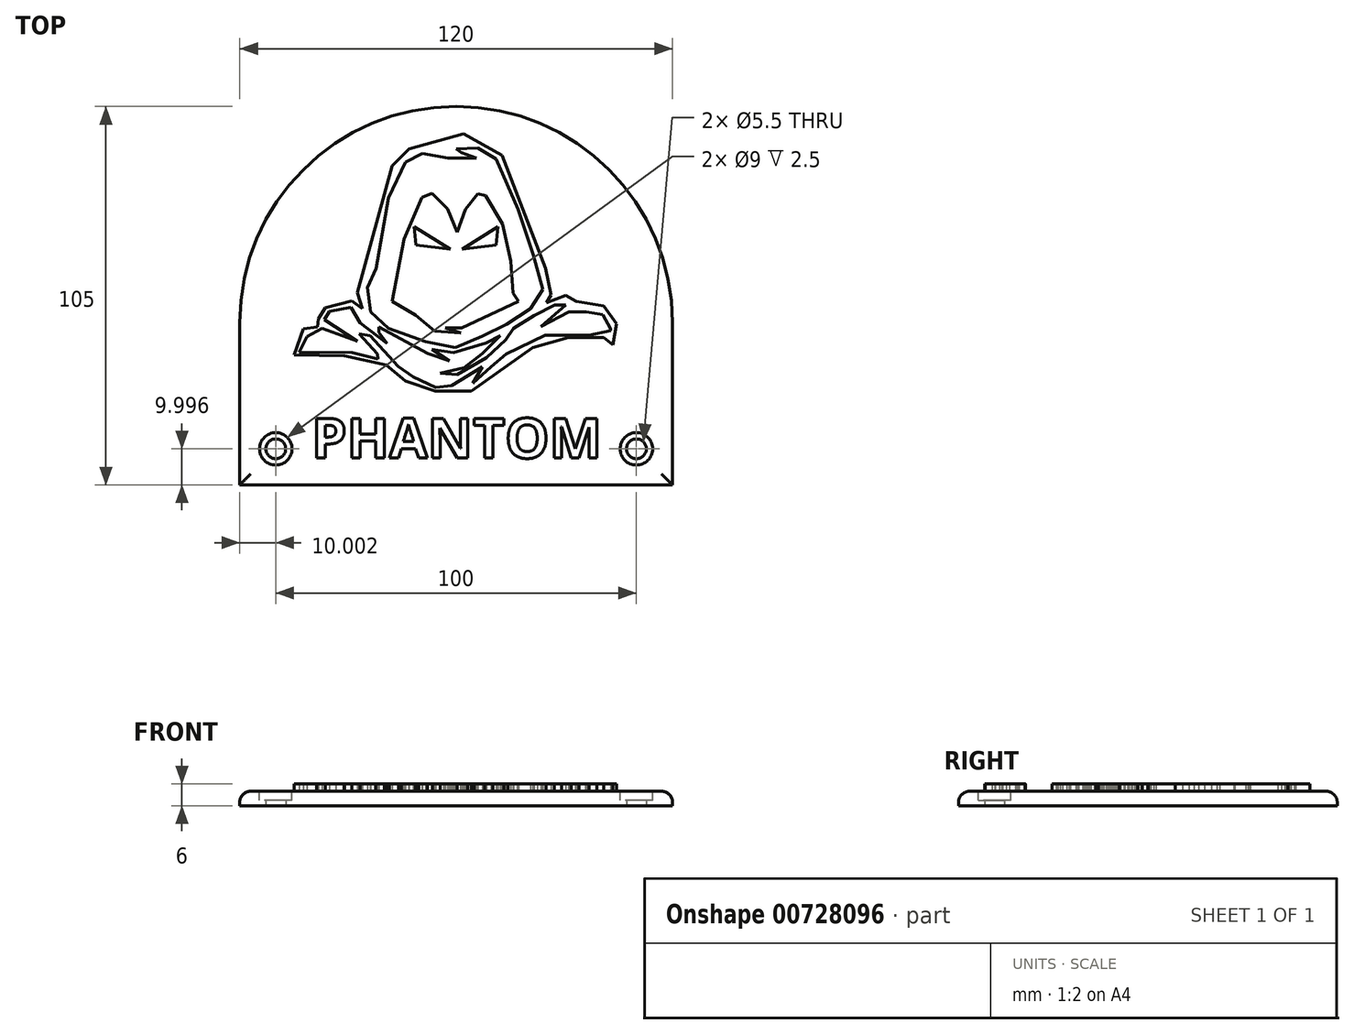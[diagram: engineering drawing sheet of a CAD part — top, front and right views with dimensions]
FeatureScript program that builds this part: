
annotation { "Feature Type Name" : "Feature", "Feature Type Description" : "" }
export const myFeature = defineFeature(function(context is Context, id is Id, definition is map)
    precondition{}
    {
        {
            var Q0;
            Q0=qCreatedBy(makeId("Top.planeOp"),FACE);
            var sketch = newSketch(context, id + "F0", { "sketchPlane" : qUnion([Q0])});
            skLineSegment(sketch, "E0", {"start": v(0.61, 84.34) * mm, "end": v(0.61, -59.17) * mm, "construction": true});
            skLineSegment(sketch, "E1", {"start": v(-44.33, 15.39) * mm, "end": v(-41.76, 22.7) * mm});
            skLineSegment(sketch, "E2", {"start": v(-41.76, 22.7) * mm, "end": v(-37.82, 23.18) * mm});
            skLineSegment(sketch, "E3", {"start": v(-37.82, 23.18) * mm, "end": v(-37.51, 25.44) * mm});
            skLineSegment(sketch, "E4", {"start": v(-37.51, 25.44) * mm, "end": v(-35.7, 28.5) * mm});
            skLineSegment(sketch, "E5", {"start": v(-26.83, 32.69) * mm, "end": v(-17.13, 67.8) * mm});
            skLineSegment(sketch, "E6", {"start": v(-17.13, 67.8) * mm, "end": v(-12.44, 72.5) * mm});
            skLineSegment(sketch, "E7", {"start": v(-12.44, 72.5) * mm, "end": v(2.64, 76.76) * mm});
            skLineSegment(sketch, "E8", {"start": v(2.64, 76.76) * mm, "end": v(13.31, 70.7) * mm});
            skLineSegment(sketch, "E9", {"start": v(13.31, 70.7) * mm, "end": v(25.4, 39.43) * mm});
            skLineSegment(sketch, "E10", {"start": v(25.4, 39.43) * mm, "end": v(26.91, 32) * mm});
            skLineSegment(sketch, "E11", {"start": v(31, 31.86) * mm, "end": v(33.88, 30.23) * mm});
            skLineSegment(sketch, "E12", {"start": v(33.88, 30.23) * mm, "end": v(41.55, 29.03) * mm});
            skLineSegment(sketch, "E13", {"start": v(41.55, 29.03) * mm, "end": v(45.06, 23.98) * mm});
            skLineSegment(sketch, "E14", {"start": v(45.06, 23.98) * mm, "end": v(44.14, 18.15) * mm});
            skLineSegment(sketch, "E15", {"start": v(44.14, 18.15) * mm, "end": v(41.5, 20.21) * mm});
            skLineSegment(sketch, "E16", {"start": v(41.5, 20.21) * mm, "end": v(31.77, 20.21) * mm});
            skLineSegment(sketch, "E17", {"start": v(31.77, 20.21) * mm, "end": v(21.89, 17.46) * mm});
            skLineSegment(sketch, "E18", {"start": v(21.89, 17.46) * mm, "end": v(4.8, 5.31) * mm});
            skLineSegment(sketch, "E19", {"start": v(4.8, 5.31) * mm, "end": v(-5.19, 5.31) * mm});
            skLineSegment(sketch, "E20", {"start": v(-5.19, 5.31) * mm, "end": v(-13.4, 8.22) * mm});
            skLineSegment(sketch, "E21", {"start": v(-13.4, 8.22) * mm, "end": v(-18.73, 12.62) * mm});
            skLineSegment(sketch, "E22", {"start": v(-18.73, 12.62) * mm, "end": v(-30.3, 15.17) * mm});
            skLineSegment(sketch, "E23", {"start": v(-30.3, 15.17) * mm, "end": v(-44.33, 15.39) * mm});
            skLineSegment(sketch, "E24", {"start": v(0.61, 72.55) * mm, "end": v(6.59, 72.8) * mm});
            skLineSegment(sketch, "E25", {"start": v(6.59, 72.8) * mm, "end": v(11.77, 69.75) * mm});
            skLineSegment(sketch, "E26", {"start": v(11.77, 69.75) * mm, "end": v(17.81, 55.78) * mm});
            skLineSegment(sketch, "E27", {"start": v(17.81, 55.78) * mm, "end": v(21.98, 43.27) * mm});
            skLineSegment(sketch, "E28", {"start": v(21.98, 43.27) * mm, "end": v(24.67, 33.51) * mm});
            skLineSegment(sketch, "E29", {"start": v(24.67, 33.51) * mm, "end": v(21.25, 28.17) * mm});
            skLineSegment(sketch, "E30", {"start": v(21.25, 28.17) * mm, "end": v(14.66, 23.95) * mm});
            skLineSegment(sketch, "E31", {"start": v(14.66, 23.95) * mm, "end": v(7.96, 20.56) * mm});
            skLineSegment(sketch, "E32", {"start": v(7.96, 20.56) * mm, "end": v(0.4, 17.4) * mm});
            skLineSegment(sketch, "E33", {"start": v(0.4, 17.4) * mm, "end": v(-7.82, 19.08) * mm});
            skLineSegment(sketch, "E34", {"start": v(-7.82, 19.08) * mm, "end": v(-18.1, 22.8) * mm});
            skLineSegment(sketch, "E35", {"start": v(-18.1, 22.8) * mm, "end": v(-23.1, 27.36) * mm});
            skLineSegment(sketch, "E36", {"start": v(-23.1, 27.36) * mm, "end": v(-23.94, 34.05) * mm});
            skLineSegment(sketch, "E37", {"start": v(-23.94, 34.05) * mm, "end": v(-21.53, 39.35) * mm});
            skLineSegment(sketch, "E38", {"start": v(-21.53, 39.35) * mm, "end": v(-18.09, 59) * mm});
            skLineSegment(sketch, "E39", {"start": v(-18.09, 59) * mm, "end": v(-13.44, 68.83) * mm});
            skLineSegment(sketch, "E40", {"start": v(-13.44, 68.83) * mm, "end": v(-8.79, 71.27) * mm});
            skLineSegment(sketch, "E41", {"start": v(-8.79, 71.27) * mm, "end": v(-1.62, 70.03) * mm});
            skLineSegment(sketch, "E42", {"start": v(-1.62, 70.03) * mm, "end": v(6.22, 70.03) * mm});
            skLineSegment(sketch, "E43", {"start": v(6.22, 70.03) * mm, "end": v(2.06, 71.54) * mm});
            skLineSegment(sketch, "E44", {"start": v(0.61, 72.55) * mm, "end": v(2.06, 71.54) * mm});
            skLineSegment(sketch, "E45", {"start": v(0.94, 49.47) * mm, "end": v(3.2, 55.73) * mm});
            skLineSegment(sketch, "E46", {"start": v(3.2, 55.73) * mm, "end": v(6.62, 60.11) * mm});
            skLineSegment(sketch, "E47", {"start": v(6.62, 60.11) * mm, "end": v(8.83, 59.61) * mm});
            skLineSegment(sketch, "E48", {"start": v(8.83, 59.61) * mm, "end": v(13.43, 51.77) * mm});
            skLineSegment(sketch, "E49", {"start": v(13.43, 51.77) * mm, "end": v(15.78, 41.46) * mm});
            skLineSegment(sketch, "E50", {"start": v(15.78, 41.46) * mm, "end": v(16.45, 32.6) * mm});
            skLineSegment(sketch, "E51", {"start": v(16.45, 32.6) * mm, "end": v(17.94, 30.21) * mm});
            skLineSegment(sketch, "E52", {"start": v(17.94, 30.21) * mm, "end": v(2.26, 22.88) * mm});
            skLineSegment(sketch, "E53", {"start": v(2.26, 22.88) * mm, "end": v(-2.4, 22.88) * mm});
            skLineSegment(sketch, "E54", {"start": v(-2.4, 22.88) * mm, "end": v(1.92, 21.49) * mm});
            skLineSegment(sketch, "E55", {"start": v(1.92, 21.49) * mm, "end": v(-5.32, 22.04) * mm});
            skLineSegment(sketch, "E56", {"start": v(-5.32, 22.04) * mm, "end": v(-10.65, 26.44) * mm});
            skLineSegment(sketch, "E57", {"start": v(-10.65, 26.44) * mm, "end": v(-17.16, 30.25) * mm});
            skLineSegment(sketch, "E58", {"start": v(-17.16, 30.25) * mm, "end": v(-13.86, 47.58) * mm});
            skLineSegment(sketch, "E59", {"start": v(-13.86, 47.58) * mm, "end": v(-8.85, 59.04) * mm});
            skLineSegment(sketch, "E60", {"start": v(-8.85, 59.04) * mm, "end": v(-6.05, 60.26) * mm});
            skLineSegment(sketch, "E61", {"start": v(-6.05, 60.26) * mm, "end": v(-1.72, 55.9) * mm});
            skLineSegment(sketch, "E62", {"start": v(-1.72, 55.9) * mm, "end": v(0.94, 49.47) * mm});
            skLineSegment(sketch, "E63", {"start": v(-42.95, 16.1) * mm, "end": v(-40.7, 20.49) * mm});
            skLineSegment(sketch, "E64", {"start": v(-40.7, 20.49) * mm, "end": v(-36.57, 22.8) * mm});
            skLineSegment(sketch, "E65", {"start": v(-36.57, 22.8) * mm, "end": v(-26.8, 19.17) * mm});
            skLineSegment(sketch, "E66", {"start": v(-26.8, 19.17) * mm, "end": v(-35.97, 25.21) * mm});
            skLineSegment(sketch, "E67", {"start": v(-35.97, 25.21) * mm, "end": v(-34.45, 27.52) * mm});
            skLineSegment(sketch, "E68", {"start": v(-34.45, 27.52) * mm, "end": v(-28.48, 28.55) * mm});
            skLineSegment(sketch, "E69", {"start": v(-28.48, 28.55) * mm, "end": v(-25.97, 24.25) * mm});
            skLineSegment(sketch, "E70", {"start": v(-25.97, 24.25) * mm, "end": v(-18.5, 18.56) * mm});
            skLineSegment(sketch, "E71", {"start": v(-18.5, 18.56) * mm, "end": v(-20.76, 21.64) * mm});
            skLineSegment(sketch, "E72", {"start": v(-20.76, 21.64) * mm, "end": v(-20.76, 23.14) * mm});
            skLineSegment(sketch, "E73", {"start": v(-20.76, 23.14) * mm, "end": v(-7.14, 15.77) * mm});
            skLineSegment(sketch, "E74", {"start": v(-7.14, 15.77) * mm, "end": v(-1.22, 13.77) * mm});
            skLineSegment(sketch, "E75", {"start": v(-1.22, 13.77) * mm, "end": v(-6, 16.92) * mm});
            skLineSegment(sketch, "E76", {"start": v(-6, 16.92) * mm, "end": v(-0.08, 16.02) * mm});
            skLineSegment(sketch, "E77", {"start": v(-0.08, 16.02) * mm, "end": v(8.86, 18.74) * mm});
            skLineSegment(sketch, "E78", {"start": v(8.86, 18.74) * mm, "end": v(12.84, 20.76) * mm});
            skLineSegment(sketch, "E79", {"start": v(12.84, 20.76) * mm, "end": v(7.89, 15.81) * mm});
            skLineSegment(sketch, "E80", {"start": v(7.89, 15.81) * mm, "end": v(2.8, 11.81) * mm});
            skLineSegment(sketch, "E81", {"start": v(2.8, 11.81) * mm, "end": v(-3.83, 10.34) * mm});
            skLineSegment(sketch, "E82", {"start": v(-3.83, 10.34) * mm, "end": v(0.96, 9.96) * mm});
            skLineSegment(sketch, "E83", {"start": v(0.96, 9.96) * mm, "end": v(9.03, 14.67) * mm});
            skLineSegment(sketch, "E84", {"start": v(9.03, 14.67) * mm, "end": v(14.4, 19.6) * mm});
            skLineSegment(sketch, "E85", {"start": v(14.4, 19.6) * mm, "end": v(16.5, 22.8) * mm});
            skLineSegment(sketch, "E86", {"start": v(16.5, 22.8) * mm, "end": v(22.25, 26.26) * mm});
            skLineSegment(sketch, "E87", {"start": v(22.25, 26.26) * mm, "end": v(27.98, 29.23) * mm});
            skLineSegment(sketch, "E88", {"start": v(27.98, 29.23) * mm, "end": v(31.07, 29.23) * mm});
            skLineSegment(sketch, "E89", {"start": v(31.07, 29.23) * mm, "end": v(24.1, 23.24) * mm});
            skLineSegment(sketch, "E90", {"start": v(24.1, 23.24) * mm, "end": v(31.89, 27.3) * mm});
            skLineSegment(sketch, "E91", {"start": v(31.89, 27.3) * mm, "end": v(36.77, 27.3) * mm});
            skLineSegment(sketch, "E92", {"start": v(36.77, 27.3) * mm, "end": v(41.35, 26.55) * mm});
            skLineSegment(sketch, "E93", {"start": v(41.35, 26.55) * mm, "end": v(43.48, 22.66) * mm});
            skLineSegment(sketch, "E94", {"start": v(43.48, 22.66) * mm, "end": v(43.48, 22.15) * mm});
            skLineSegment(sketch, "E95", {"start": v(43.48, 22.15) * mm, "end": v(37.45, 20.9) * mm});
            skLineSegment(sketch, "E96", {"start": v(37.45, 20.9) * mm, "end": v(25.3, 20.9) * mm});
            skLineSegment(sketch, "E97", {"start": v(25.3, 20.9) * mm, "end": v(14.46, 15.71) * mm});
            skLineSegment(sketch, "E98", {"start": v(14.46, 15.71) * mm, "end": v(10.3, 12.03) * mm});
            skLineSegment(sketch, "E99", {"start": v(10.3, 12.03) * mm, "end": v(5.3, 7.5) * mm});
            skLineSegment(sketch, "E100", {"start": v(5.3, 7.5) * mm, "end": v(7.87, 12.14) * mm});
            skLineSegment(sketch, "E101", {"start": v(7.87, 12.14) * mm, "end": v(-0.6, 6.9) * mm});
            skLineSegment(sketch, "E102", {"start": v(-0.6, 6.9) * mm, "end": v(-5.05, 6.42) * mm});
            skLineSegment(sketch, "E103", {"start": v(-5.05, 6.42) * mm, "end": v(-11.3, 9.28) * mm});
            skLineSegment(sketch, "E104", {"start": v(-11.3, 9.28) * mm, "end": v(-15.41, 12.25) * mm});
            skLineSegment(sketch, "E105", {"start": v(-15.41, 12.25) * mm, "end": v(-23.25, 20.75) * mm});
            skLineSegment(sketch, "E106", {"start": v(-23.25, 20.75) * mm, "end": v(-26.26, 21.21) * mm});
            skLineSegment(sketch, "E107", {"start": v(-26.26, 21.21) * mm, "end": v(-21.2, 15.63) * mm});
            skLineSegment(sketch, "E108", {"start": v(-21.2, 15.63) * mm, "end": v(-21.04, 14.2) * mm});
            skLineSegment(sketch, "E109", {"start": v(-21.04, 14.2) * mm, "end": v(-28.1, 16.06) * mm});
            skLineSegment(sketch, "E110", {"start": v(-28.1, 16.06) * mm, "end": v(-42.95, 16.1) * mm});
            skLineSegment(sketch, "E111", {"start": v(31, 31.86) * mm, "end": v(25.71, 29.85) * mm});
            skLineSegment(sketch, "E112", {"start": v(25.71, 29.85) * mm, "end": v(26.91, 32) * mm});
            skLineSegment(sketch, "E113", {"start": v(-26.83, 32.69) * mm, "end": v(-25.34, 28.24) * mm});
            skLineSegment(sketch, "E114", {"start": v(-25.34, 28.24) * mm, "end": v(-28.23, 30.36) * mm});
            skLineSegment(sketch, "E115", {"start": v(-28.23, 30.36) * mm, "end": v(-35.7, 28.5) * mm});
            skLineSegment(sketch, "E116", {"start": v(-59.39, -0.66) * mm, "end": v(-59.39, 84.34) * mm});
            skLineSegment(sketch, "E117", {"start": v(-59.39, 84.34) * mm, "end": v(60.61, 84.34) * mm});
            skLineSegment(sketch, "E118", {"start": v(60.61, 84.34) * mm, "end": v(60.61, -0.66) * mm});
            skLineSegment(sketch, "E119.0", {"start": v(-6, 16.92) * mm, "end": v(0.96, 9.96) * mm, "construction": true});
            skLineSegment(sketch, "E120.0", {"start": v(7.89, 15.81) * mm, "end": v(9.03, 14.67) * mm, "construction": true});
            skLineSegment(sketch, "E121.0", {"start": v(-28.48, 28.55) * mm, "end": v(-18.5, 18.56) * mm, "construction": true});
            skLineSegment(sketch, "E122.0", {"start": v(2.06, 71.54) * mm, "end": v(3.56, 70.03) * mm, "construction": true});
            skLineSegment(sketch, "E123.0", {"start": v(14.46, 15.71) * mm, "end": v(27.98, 29.23) * mm, "construction": true});
            skLineSegment(sketch, "E124.0", {"start": v(0.96, 9.96) * mm, "end": v(2.8, 11.81) * mm, "construction": true});
            skLineSegment(sketch, "E125.0", {"start": v(-7.14, 15.77) * mm, "end": v(-6, 16.92) * mm, "construction": true});
            skLineSegment(sketch, "E126.0", {"start": v(-40.7, 20.49) * mm, "end": v(-35.97, 25.21) * mm, "construction": true});
            skLineSegment(sketch, "E127.trimOffspring", {"start": v(0.4, 17.4) * mm, "end": v(0.61, 17.2) * mm, "construction": true});
            skText(sketch, "E128", { "text": "PHANTOM", "fontName": "OpenSans-Bold.ttf"});
            skLineSegment(sketch, "E129.top", {"start": v(-59.39, -20.66) * mm, "end": v(60.61, -20.66) * mm});
            skLineSegment(sketch, "E129.left", {"start": v(-59.39, -0.66) * mm, "end": v(-59.39, -20.66) * mm});
            skLineSegment(sketch, "E129.right", {"start": v(60.61, -0.66) * mm, "end": v(60.61, -20.66) * mm});
            skCircle(sketch, "E130", {"center": v(-49.39, -10.66) * mm, "radius": 2.75 * mm});
            skCircle(sketch, "E131.MirrorC", {"center": v(50.61, -10.66) * mm, "radius": 2.75 * mm});
            skLineSegment(sketch, "E132", {"start": v(-11, 50.95) * mm, "end": v(-1.03, 44.68) * mm});
            skLineSegment(sketch, "E133", {"start": v(-1.03, 44.68) * mm, "end": v(-10.52, 45.92) * mm});
            skLineSegment(sketch, "E134", {"start": v(-10.52, 45.92) * mm, "end": v(-11, 50.95) * mm});
            skLineSegment(sketch, "E135.MirrorCS", {"start": v(11.74, 45.92) * mm, "end": v(12.22, 50.95) * mm});
            skLineSegment(sketch, "E136.MirrorCS", {"start": v(2.26, 44.68) * mm, "end": v(11.74, 45.92) * mm});
            skLineSegment(sketch, "E137.MirrorCS", {"start": v(12.22, 50.95) * mm, "end": v(2.26, 44.68) * mm});
            const initialGuessF0  = {"E128": [-0.03939, -0.01323, 1, 0, 0.0111]};
            skSetInitialGuess(sketch, initialGuessF0);
            skSolve(sketch);
        }
        {
            var Q0;
            Q0=makeQuery(id+"F0.imprint","IMPRINT",FACE,{"disambiguationData":[TD([[makeQuery(id+"F0.imprint","IMPRINT",EDGE,{"derivedFrom":sQuery(id+"F0.wireOp",EDGE,"E1")}),1.0]])]});
            var Q1;
            Q1=makeQuery(id+"F0.imprint","IMPRINT",FACE,{"disambiguationData":[TD([[makeQuery(id+"F0.imprint","IMPRINT",EDGE,{"derivedFrom":sQuery(id+"F0.wireOp",EDGE,"E128.sketch_text.stroke-76")}),-1.0]])]});
            var Q2;
            Q2=makeQuery(id+"F0.imprint","IMPRINT",FACE,{"disambiguationData":[TD([[makeQuery(id+"F0.imprint","IMPRINT",EDGE,{"derivedFrom":sQuery(id+"F0.wireOp",EDGE,"E128.sketch_text.stroke-0")}),-1.0]])]});
            var Q3;
            Q3=makeQuery(id+"F0.imprint","IMPRINT",FACE,{"disambiguationData":[TD([[makeQuery(id+"F0.imprint","IMPRINT",EDGE,{"derivedFrom":sQuery(id+"F0.wireOp",EDGE,"E128.sketch_text.stroke-62")}),-1.0]])]});
            var Q4;
            Q4=makeQuery(id+"F0.imprint","IMPRINT",FACE,{"disambiguationData":[TD([[makeQuery(id+"F0.imprint","IMPRINT",EDGE,{"derivedFrom":sQuery(id+"F0.wireOp",EDGE,"E128.sketch_text.stroke-28")}),-1.0]])]});
            var Q5;
            Q5=makeQuery(id+"F0.imprint","IMPRINT",FACE,{"disambiguationData":[TD([[makeQuery(id+"F0.imprint","IMPRINT",EDGE,{"derivedFrom":sQuery(id+"F0.wireOp",EDGE,"ixal4Lwa-Dh1c-fVBC-PDmB-XkwGghMvrbmg")}),-1.0]])]});
            var Q6;
            Q6=makeQuery(id+"F0.imprint","IMPRINT",FACE,{"disambiguationData":[TD([[makeQuery(id+"F0.imprint","IMPRINT",EDGE,{"derivedFrom":sQuery(id+"F0.wireOp",EDGE,"E45")}),-1.0]])]});
            var Q7;
            Q7=makeQuery(id+"F0.imprint","IMPRINT",FACE,{"disambiguationData":[TD([[makeQuery(id+"F0.imprint","IMPRINT",EDGE,{"derivedFrom":sQuery(id+"F0.wireOp",EDGE,"E63")}),-1.0]])]});
            var Q8;
            Q8=makeQuery(id+"F0.imprint","IMPRINT",FACE,{"disambiguationData":[TD([[makeQuery(id+"F0.imprint","IMPRINT",EDGE,{"derivedFrom":sQuery(id+"F0.wireOp",EDGE,"E128.sketch_text.stroke-70")}),1.0]])]});
            var Q9;
            Q9=makeQuery(id+"F0.imprint","IMPRINT",FACE,{"disambiguationData":[TD([[makeQuery(id+"F0.imprint","IMPRINT",EDGE,{"derivedFrom":sQuery(id+"F0.wireOp",EDGE,"E128.sketch_text.stroke-54")}),-1.0]])]});
            var Q10;
            Q10=makeQuery(id+"F0.imprint","IMPRINT",FACE,{"disambiguationData":[TD([[makeQuery(id+"F0.imprint","IMPRINT",EDGE,{"derivedFrom":sQuery(id+"F0.wireOp",EDGE,"E128.sketch_text.stroke-0")}),1.0]])]});
            var Q11;
            Q11=makeQuery(id+"F0.imprint","IMPRINT",FACE,{"disambiguationData":[TD([[makeQuery(id+"F0.imprint","IMPRINT",EDGE,{"derivedFrom":sQuery(id+"F0.wireOp",EDGE,"E24")}),-1.0]])]});
            var Q12;
            Q12=makeQuery(id+"F0.imprint","IMPRINT",FACE,{"disambiguationData":[TD([[makeQuery(id+"F0.imprint","IMPRINT",EDGE,{"derivedFrom":sQuery(id+"F0.wireOp",EDGE,"E1")}),-1.0]])]});
            var Q13;
            Q13=makeQuery(id+"F0.imprint","IMPRINT",FACE,{"disambiguationData":[TD([[makeQuery(id+"F0.imprint","IMPRINT",EDGE,{"derivedFrom":sQuery(id+"F0.wireOp",EDGE,"E128.sketch_text.stroke-16")}),-1.0]])]});
            var Q14;
            Q14=makeQuery(id+"F0.imprint","IMPRINT",FACE,{"disambiguationData":[TD([[makeQuery(id+"F0.imprint","IMPRINT",EDGE,{"derivedFrom":sQuery(id+"F0.wireOp",EDGE,"r933fQ9t-bKuE-JaNL-tnma-PBr1p5SVssM0")}),1.0]])]});
            var Q15;
            Q15=makeQuery(id+"F0.imprint","IMPRINT",FACE,{"disambiguationData":[TD([[makeQuery(id+"F0.imprint","IMPRINT",EDGE,{"derivedFrom":sQuery(id+"F0.wireOp",EDGE,"E128.sketch_text.stroke-40")}),-1.0]])]});
            var Q16;
            Q16=makeQuery(id+"F0.imprint","IMPRINT",FACE,{"disambiguationData":[TD([[makeQuery(id+"F0.imprint","IMPRINT",EDGE,{"derivedFrom":sQuery(id+"F0.wireOp",EDGE,"E128.sketch_text.stroke-36")}),1.0]])]});
            var Q17;
            Q17=makeQuery(id+"F0.imprint","IMPRINT",FACE,{"disambiguationData":[TD([[makeQuery(id+"F0.imprint","IMPRINT",EDGE,{"derivedFrom":sQuery(id+"F0.wireOp",EDGE,"E132")}),-1.0]])]});
            var Q18;
            Q18=makeQuery(id+"F0.imprint","IMPRINT",FACE,{"disambiguationData":[TD([[makeQuery(id+"F0.imprint","IMPRINT",EDGE,{"derivedFrom":sQuery(id+"F0.wireOp",EDGE,"9HaLUQFe-ZPNq-Nkvr-l6tD-eBDGtd3K5vBT")}),-1.0]])]});
            var Q19;
            Q19=makeQuery(id+"F0.imprint","IMPRINT",FACE,{"disambiguationData":[TD([[makeQuery(id+"F0.imprint","IMPRINT",EDGE,{"derivedFrom":sQuery(id+"F0.wireOp",EDGE,"E135.MirrorCS")}),1.0]])]});
            extrude(context, id + "F1", {"entities" : qUnion([Q0, Q1, Q2, Q3, Q4, Q5, Q6, Q7, Q8, Q9, Q10, Q11, Q12, Q13, Q14, Q15, Q16, Q17, Q18, Q19]), "depth" : 4 * mm, "offsetDistance" : 25 * mm});
        }
        {
            var Q0;
            {var subQ10=sQuery(id+"F0.wireOp",EDGE,"E129.top");var subQ12=sQuery(id+"F0.wireOp",EDGE,"E129.right");var subQ13=sQuery(id+"F0.wireOp",EDGE,"E118");var subQ16=sQuery(id+"F0.wireOp",EDGE,"E117");var subQ17=makeQuery(id+"F1.opExtrude","SWEPT_FACE",FACE,{"disambiguationData":[OSD([subQ16])]});var subQ19=sQuery(id+"F0.wireOp",EDGE,"E129.left");var subQ20=sQuery(id+"F0.wireOp",EDGE,"E116");var subQ25=sQuery(id+"F0.wireOp",EDGE,"E130");var subQ28=sQuery(id+"F0.wireOp",EDGE,"E131.MirrorC");Q0=makeQuery(id+"F4.boolean.opBoolean","SPLIT",FACE,{"disambiguationData":[TD([subQ17])],"derivedFrom":makeQuery(id+"F3.boolean.opBoolean","SPLIT",FACE,{"disambiguationData":[TD([subQ17])],"derivedFrom":makeQuery(id+"F1.opExtrude","CAP_FACE",FACE,{"disambiguationData":[OSD([subQ20,subQ16,subQ13,subQ10,subQ19,subQ12,subQ25,subQ28])],"isStart":false})})});}
            var sketch = newSketch(context, id + "F2", { "sketchPlane" : qUnion([Q0])});
            skCircle(sketch, "E138", {"center": v(-49.39, -10.66) * mm, "radius": 4.5 * mm});
            skCircle(sketch, "E139", {"center": v(50.61, -10.66) * mm, "radius": 4.5 * mm});
            skSolve(sketch);
        }
        {
            var Q0;
            Q0=makeQuery(id+"F0.imprint","IMPRINT",FACE,{"disambiguationData":[TD([[makeQuery(id+"F0.imprint","IMPRINT",EDGE,{"derivedFrom":sQuery(id+"F0.wireOp",EDGE,"E1")}),-1.0]])]});
            var Q1;
            Q1=makeQuery(id+"F0.imprint","IMPRINT",FACE,{"disambiguationData":[TD([[makeQuery(id+"F0.imprint","IMPRINT",EDGE,{"derivedFrom":sQuery(id+"F0.wireOp",EDGE,"E45")}),-1.0]])]});
            extrude(context, id + "F3", {"entities" : qUnion([Q0, Q1]), "operationType" : NewBodyOperationType.ADD, "flatOperationType" : FlatOperationType.REMOVE, "depth" : 6 * mm, "offsetDistance" : 25 * mm, "domain" : OperationDomain.MODEL});
        }
        {
            var Q0;
            Q0=makeQuery(id+"F0.imprint","IMPRINT",FACE,{"disambiguationData":[TD([[makeQuery(id+"F0.imprint","IMPRINT",EDGE,{"derivedFrom":sQuery(id+"F0.wireOp",EDGE,"E128.sketch_text.stroke-0")}),-1.0]])]});
            var Q1;
            Q1=makeQuery(id+"F0.imprint","IMPRINT",FACE,{"disambiguationData":[TD([[makeQuery(id+"F0.imprint","IMPRINT",EDGE,{"derivedFrom":sQuery(id+"F0.wireOp",EDGE,"E128.sketch_text.stroke-16")}),-1.0]])]});
            var Q2;
            Q2=makeQuery(id+"F0.imprint","IMPRINT",FACE,{"disambiguationData":[TD([[makeQuery(id+"F0.imprint","IMPRINT",EDGE,{"derivedFrom":sQuery(id+"F0.wireOp",EDGE,"E128.sketch_text.stroke-28")}),-1.0]])]});
            var Q3;
            Q3=makeQuery(id+"F0.imprint","IMPRINT",FACE,{"disambiguationData":[TD([[makeQuery(id+"F0.imprint","IMPRINT",EDGE,{"derivedFrom":sQuery(id+"F0.wireOp",EDGE,"E128.sketch_text.stroke-40")}),-1.0]])]});
            var Q4;
            Q4=makeQuery(id+"F0.imprint","IMPRINT",FACE,{"disambiguationData":[TD([[makeQuery(id+"F0.imprint","IMPRINT",EDGE,{"derivedFrom":sQuery(id+"F0.wireOp",EDGE,"E128.sketch_text.stroke-54")}),-1.0]])]});
            var Q5;
            Q5=makeQuery(id+"F0.imprint","IMPRINT",FACE,{"disambiguationData":[TD([[makeQuery(id+"F0.imprint","IMPRINT",EDGE,{"derivedFrom":sQuery(id+"F0.wireOp",EDGE,"E128.sketch_text.stroke-62")}),-1.0]])]});
            var Q6;
            Q6=makeQuery(id+"F0.imprint","IMPRINT",FACE,{"disambiguationData":[TD([[makeQuery(id+"F0.imprint","IMPRINT",EDGE,{"derivedFrom":sQuery(id+"F0.wireOp",EDGE,"E128.sketch_text.stroke-76")}),-1.0]])]});
            extrude(context, id + "F4", {"entities" : qUnion([Q0, Q1, Q2, Q3, Q4, Q5, Q6]), "operationType" : NewBodyOperationType.ADD, "flatOperationType" : FlatOperationType.REMOVE, "depth" : 6 * mm, "offsetDistance" : 25 * mm, "domain" : OperationDomain.MODEL});
        }
        {
            var Q0;
            Q0 = qSketchRegion(id + "F2", true);
            extrude(context, id + "F5", {"entities" : qUnion([Q0]), "operationType" : NewBodyOperationType.REMOVE, "oppositeDirection" : true, "depth" : 2.5 * mm, "offsetDistance" : 25 * mm});
        }
        {
            var Q0;
            Q0=makeQuery(id+"F1.opExtrude","CAP_EDGE",EDGE,{"disambiguationData":[OSD([sQuery(id+"F0.wireOp",EDGE,"6Twr0VLn-Kq2v-9dmt-LS42-5jNN3DOIOGF8")])],"isStart":false});
            var Q1;
            Q1=makeQuery(id+"F1.opExtrude","CAP_EDGE",EDGE,{"disambiguationData":[OSD([sQuery(id+"F0.wireOp",EDGE,"H6YuyeC9-d0xV-tLW2-SV9e-pPCP5sKM99fR")])],"isStart":false});
            var Q2;
            Q2=makeQuery(id+"F1.opExtrude","CAP_EDGE",EDGE,{"disambiguationData":[OSD([sQuery(id+"F0.wireOp",EDGE,"edSUIHol-hNC8-TOqC-sSjQ-9aSgyO3oAdcl")])],"isStart":false});
            var Q3;
            Q3=makeQuery(id+"F1.opExtrude","CAP_EDGE",EDGE,{"disambiguationData":[OSD([sQuery(id+"F0.wireOp",EDGE,"E116")])],"isStart":false});
            var Q4;
            Q4=makeQuery(id+"F1.opExtrude","CAP_EDGE",EDGE,{"disambiguationData":[OSD([sQuery(id+"F0.wireOp",EDGE,"E117")])],"isStart":false});
            var Q5;
            Q5=makeQuery(id+"F1.opExtrude","CAP_EDGE",EDGE,{"disambiguationData":[OSD([sQuery(id+"F0.wireOp",EDGE,"E118")])],"isStart":false});
            var Q6;
            Q6=makeQuery(id+"F1.opExtrude","CAP_EDGE",EDGE,{"disambiguationData":[OSD([sQuery(id+"F0.wireOp",EDGE,"E129.top")])],"isStart":false});
            fillet(context, id + "F6", {"entities" : qUnion([Q0, Q1, Q2, Q3, Q4, Q5, Q6]), "radius" : 3 * mm, "tangentPropagation" : true, "allowEdgeOverflow" : false});
        }
        {
            var Q0;
            Q0=makeQuery(id+"F1.opExtrude","SWEPT_EDGE",EDGE,{"disambiguationData":[OSD([sQuery(id+"F0.wireOp",EDGE,"E116"),sQuery(id+"F0.wireOp",EDGE,"E117")])]});
            var Q1;
            Q1=makeQuery(id+"F1.opExtrude","SWEPT_EDGE",EDGE,{"disambiguationData":[OSD([sQuery(id+"F0.wireOp",EDGE,"E117"),sQuery(id+"F0.wireOp",EDGE,"E118")])]});
            fillet(context, id + "F7", {"entities" : qUnion([Q0, Q1]), "radius" : 60 * mm, "tangentPropagation" : true, "allowEdgeOverflow" : false});
        }
    });
